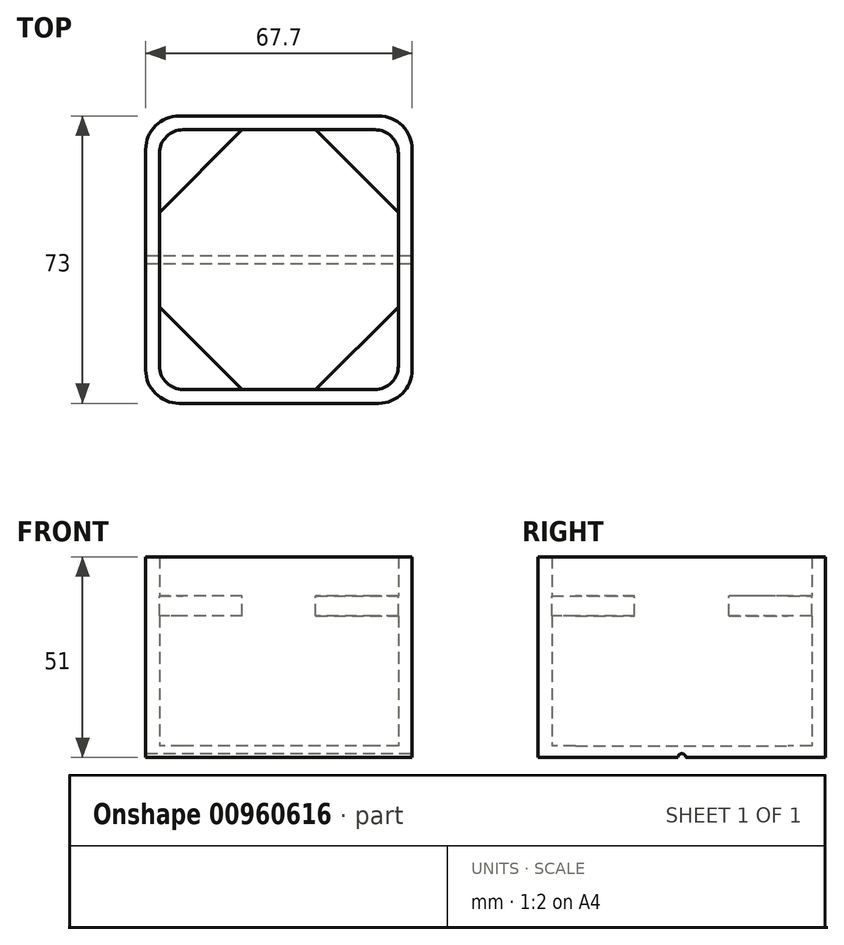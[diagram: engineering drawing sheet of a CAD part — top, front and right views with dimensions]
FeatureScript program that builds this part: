
annotation { "Feature Type Name" : "Feature", "Feature Type Description" : "" }
export const myFeature = defineFeature(function(context is Context, id is Id, definition is map)
    precondition{}
    {
        {
            var Q0;
            Q0=qCreatedBy(makeId("Top.planeOp"),FACE);
            var sketch = newSketch(context, id + "F0", { "sketchPlane" : qUnion([Q0])});
            skLineSegment(sketch, "E0.bottom", {"start": v(25.35, -36.5) * mm, "end": v(-25.35, -36.5) * mm});
            skLineSegment(sketch, "E0.top", {"start": v(25.35, 36.5) * mm, "end": v(-25.35, 36.5) * mm});
            skLineSegment(sketch, "E0.left", {"start": v(33.85, -28) * mm, "end": v(33.85, 28) * mm});
            skLineSegment(sketch, "E0.right", {"start": v(-33.85, -28) * mm, "end": v(-33.85, 28) * mm});
            skPoint(sketch, "E0.middle", {"position": v(0, 0) * mm});
            skPoint(sketch, "E1.visualSharp", {"position": v(-33.85, 36.5) * mm});
            skPoint(sketch, "E2.visualSharp", {"position": v(33.85, 36.5) * mm});
            skPoint(sketch, "E3.visualSharp", {"position": v(33.85, -36.5) * mm});
            skPoint(sketch, "E4.visualSharp", {"position": v(-33.85, -36.5) * mm});
            skArc(sketch, "E5.filletArc", {"start": v(-25.35, 36.5) * mm, "mid": v(-31.36, 34.01) * mm, "end": v(-33.85, 28) * mm});
            skArc(sketch, "E6.filletArc", {"start": v(33.85, 28) * mm, "mid": v(31.36, 34.01) * mm, "end": v(25.35, 36.5) * mm});
            skArc(sketch, "E7.filletArc", {"start": v(-33.85, -28) * mm, "mid": v(-31.36, -34.01) * mm, "end": v(-25.35, -36.5) * mm});
            skArc(sketch, "E8.filletArc", {"start": v(25.35, -36.5) * mm, "mid": v(31.36, -34.01) * mm, "end": v(33.85, -28) * mm});
            skSolve(sketch);
        }
        {
            var Q0;
            Q0=makeQuery(id+"F0.imprint","IMPRINT",FACE,{"disambiguationData":[TD([[makeQuery(id+"F0.imprint","IMPRINT",EDGE,{"derivedFrom":sQuery(id+"F0.wireOp",EDGE,"E0.bottom")}),-1.0]])]});
            extrude(context, id + "F1", {"entities" : qUnion([Q0]), "depth" : 3 * mm, "offsetDistance" : 25 * mm});
        }
        {
            var Q0;
            Q0=makeQuery(id+"F1.opExtrude","CAP_FACE",FACE,{"disambiguationData":[OSD([sQuery(id+"F0.wireOp",EDGE,"E0.bottom"),sQuery(id+"F0.wireOp",EDGE,"E0.top"),sQuery(id+"F0.wireOp",EDGE,"E0.left"),sQuery(id+"F0.wireOp",EDGE,"E0.right"),sQuery(id+"F0.wireOp",EDGE,"E1.filletArc"),sQuery(id+"F0.wireOp",EDGE,"E2.filletArc"),sQuery(id+"F0.wireOp",EDGE,"E3.filletArc"),sQuery(id+"F0.wireOp",EDGE,"E4.filletArc")])],"isStart":false});
            var sketch = newSketch(context, id + "F2", { "sketchPlane" : qUnion([Q0])});
            skLineSegment(sketch, "E9.bottom", {"start": v(24.35, -33) * mm, "end": v(-24.35, -33) * mm});
            skLineSegment(sketch, "E9.top", {"start": v(24.35, 33) * mm, "end": v(-24.35, 33) * mm});
            skLineSegment(sketch, "E9.left", {"start": v(30.35, -27) * mm, "end": v(30.35, 27) * mm});
            skLineSegment(sketch, "E9.right", {"start": v(-30.35, -27) * mm, "end": v(-30.35, 27) * mm});
            skPoint(sketch, "E9.middle", {"position": v(0, 0) * mm});
            skPoint(sketch, "E10.visualSharp", {"position": v(-30.35, 33) * mm});
            skPoint(sketch, "E11.visualSharp", {"position": v(30.35, 33) * mm});
            skPoint(sketch, "E12.visualSharp", {"position": v(-30.35, -33) * mm});
            skPoint(sketch, "E13.visualSharp", {"position": v(30.35, -33) * mm});
            skPoint(sketch, "E14", {"position": v(-22.35, 25) * mm});
            skPoint(sketch, "E15", {"position": v(22.35, 25) * mm});
            skPoint(sketch, "E16", {"position": v(22.35, -25) * mm});
            skPoint(sketch, "E17", {"position": v(-22.35, -25) * mm});
            skArc(sketch, "E18.filletArc", {"start": v(-24.35, 33) * mm, "mid": v(-28.6, 31.24) * mm, "end": v(-30.35, 27) * mm});
            skArc(sketch, "E19.filletArc", {"start": v(30.35, 27) * mm, "mid": v(28.6, 31.24) * mm, "end": v(24.35, 33) * mm});
            skArc(sketch, "E20.filletArc", {"start": v(24.35, -33) * mm, "mid": v(28.6, -31.24) * mm, "end": v(30.35, -27) * mm});
            skArc(sketch, "E21.filletArc", {"start": v(-30.35, -27) * mm, "mid": v(-28.6, -31.24) * mm, "end": v(-24.35, -33) * mm});
            skSolve(sketch);
        }
        {
            var Q0;
            Q0=makeQuery(id+"F2.imprint","IMPRINT",FACE,{"disambiguationData":[TD([[makeQuery(id+"F2.imprint","IMPRINT",EDGE,{"derivedFrom":sQuery(id+"F2.wireOp",EDGE,"E9.bottom")}),1.0]])]});
            extrude(context, id + "F3", {"entities" : qUnion([Q0]), "operationType" : NewBodyOperationType.ADD, "depth" : 38 * mm, "offsetDistance" : 25 * mm});
        }
        {
            var Q0;
            Q0=makeQuery(id+"F3.opExtrude","CAP_FACE",FACE,{"disambiguationData":[OSD([sQuery(id+"F0.wireOp",EDGE,"E0.bottom"),sQuery(id+"F0.wireOp",EDGE,"E0.top"),sQuery(id+"F0.wireOp",EDGE,"E0.left"),sQuery(id+"F0.wireOp",EDGE,"E0.right"),sQuery(id+"F0.wireOp",EDGE,"dvduAT8U-9z4F-e4AS-9eoL-lbGmKiJ1iybt"),sQuery(id+"F0.wireOp",EDGE,"aJOZrvJK-A2hF-QCfp-oE2e-V53GVGUSBUPk"),sQuery(id+"F0.wireOp",EDGE,"IG0yzDuE-LkIn-5tUI-d1jc-H29fERG7UsIG"),sQuery(id+"F0.wireOp",EDGE,"B1HQ0swq-clk5-EkSq-0daU-o4C5Dgl36Lca"),sQuery(id+"F0.wireOp",EDGE,"Mjkd7YmC-RiAe-4hFl-lhO9-aFGPjJMqciLP"),sQuery(id+"F2.wireOp",EDGE,"E9.bottom"),sQuery(id+"F2.wireOp",EDGE,"E9.top"),sQuery(id+"F2.wireOp",EDGE,"E9.left"),sQuery(id+"F2.wireOp",EDGE,"E9.right")])],"isStart":false});
            var sketch = newSketch(context, id + "F4", { "sketchPlane" : qUnion([Q0])});
            skLineSegment(sketch, "E22.bottom", {"start": v(30.35, 33) * mm, "end": v(-30.35, 33) * mm});
            skLineSegment(sketch, "E22.top", {"start": v(30.35, -33) * mm, "end": v(-30.35, -33) * mm});
            skLineSegment(sketch, "E22.left", {"start": v(30.35, 33) * mm, "end": v(30.35, -33) * mm});
            skLineSegment(sketch, "E22.right", {"start": v(-30.35, 33) * mm, "end": v(-30.35, -33) * mm});
            skPoint(sketch, "E22.middle", {"position": v(0, 0) * mm});
            skLineSegment(sketch, "E23", {"start": v(9.35, 33) * mm, "end": v(30.35, 12) * mm});
            skLineSegment(sketch, "E24", {"start": v(30.35, 12) * mm, "end": v(30.35, 27) * mm});
            skLineSegment(sketch, "E25", {"start": v(-30.35, 12) * mm, "end": v(-30.35, 27) * mm});
            skLineSegment(sketch, "E26", {"start": v(-24.35, 33) * mm, "end": v(-9.35, 33) * mm});
            skLineSegment(sketch, "E27", {"start": v(-9.35, 33) * mm, "end": v(-30.35, 12) * mm});
            skLineSegment(sketch, "E28", {"start": v(-30.35, -12) * mm, "end": v(-9.35, -33) * mm});
            skLineSegment(sketch, "E29", {"start": v(-9.35, -33) * mm, "end": v(-30.35, -33) * mm});
            skLineSegment(sketch, "E30", {"start": v(9.35, -33) * mm, "end": v(30.35, -12) * mm});
            skLineSegment(sketch, "E31", {"start": v(30.35, -12) * mm, "end": v(30.35, -27) * mm});
            skLineSegment(sketch, "E32", {"start": v(24.35, -33) * mm, "end": v(9.35, -33) * mm});
            skLineSegment(sketch, "E33", {"start": v(-30.35, -33) * mm, "end": v(-30.35, -12) * mm});
            skPoint(sketch, "E34.visualSharp", {"position": v(-30.35, 33) * mm});
            skArc(sketch, "E34.filletArc", {"start": v(-24.35, 33) * mm, "mid": v(-28.6, 31.24) * mm, "end": v(-30.35, 27) * mm});
            skPoint(sketch, "E35.visualSharp", {"position": v(30.35, -33) * mm});
            skArc(sketch, "E35.filletArc", {"start": v(24.35, -33) * mm, "mid": v(28.6, -31.24) * mm, "end": v(30.35, -27) * mm});
            skLineSegment(sketch, "E36", {"start": v(9.35, 33) * mm, "end": v(24.35, 33) * mm});
            skPoint(sketch, "E37.visualSharp", {"position": v(30.35, 33) * mm});
            skArc(sketch, "E37.filletArc", {"start": v(30.35, 27) * mm, "mid": v(28.6, 31.24) * mm, "end": v(24.35, 33) * mm});
            skLineSegment(sketch, "E38", {"start": v(-30.35, -12) * mm, "end": v(-30.35, -27) * mm});
            skLineSegment(sketch, "E39", {"start": v(-24.35, -33) * mm, "end": v(-9.35, -33) * mm});
            skPoint(sketch, "E40.visualSharp", {"position": v(-30.35, -33) * mm});
            skArc(sketch, "E40.filletArc", {"start": v(-30.35, -27) * mm, "mid": v(-28.6, -31.24) * mm, "end": v(-24.35, -33) * mm});
            skSolve(sketch);
        }
        {
            var Q0;
            Q0 = qSketchRegion(id + "F6", true);
            var Q1;
            Q1=makeQuery(id+"F4.imprint","IMPRINT",FACE,{"disambiguationData":[TD([[makeQuery(id+"F4.imprint","IMPRINT",EDGE,{"derivedFrom":makeQuery(id+"F3.opExtrude","CAP_EDGE",EDGE,{"disambiguationData":[OSD([sQuery(id+"F0.wireOp",EDGE,"E0.bottom")])],"isStart":false})}),-1.0]])]});
            var Q2;
            {var subQ0=sQuery(id+"F4.wireOp",EDGE,"E34.filletArc");Q2=makeQuery(id+"F4.imprint","IMPRINT",FACE,{"disambiguationData":[TD([[makeQuery(id+"F4.imprint","IMPRINT",EDGE,{"derivedFrom":subQ0}),-1.0]])]});}
            var Q3;
            {var subQ0=sQuery(id+"F4.wireOp",EDGE,"E37.filletArc");Q3=makeQuery(id+"F4.imprint","IMPRINT",FACE,{"disambiguationData":[TD([[makeQuery(id+"F4.imprint","IMPRINT",EDGE,{"derivedFrom":subQ0}),-1.0]])]});}
            var Q4;
            {var subQ0=sQuery(id+"F4.wireOp",EDGE,"E35.filletArc");Q4=makeQuery(id+"F4.imprint","IMPRINT",FACE,{"disambiguationData":[TD([[makeQuery(id+"F4.imprint","IMPRINT",EDGE,{"derivedFrom":subQ0}),-1.0]])]});}
            var Q5;
            {var subQ0=sQuery(id+"F4.wireOp",EDGE,"E40.filletArc");Q5=makeQuery(id+"F4.imprint","IMPRINT",FACE,{"disambiguationData":[TD([[makeQuery(id+"F4.imprint","IMPRINT",EDGE,{"derivedFrom":subQ0}),-1.0]])]});}
            var Q6;
            {var subQ2=sQuery(id+"F4.wireOp",EDGE,"E30");Q6=makeQuery(id+"F4.imprint","IMPRINT",FACE,{"disambiguationData":[TD([[makeQuery(id+"F4.imprint","IMPRINT",EDGE,{"derivedFrom":subQ2}),-1.0]])]});}
            var Q7;
            {var subQ2=sQuery(id+"F4.wireOp",EDGE,"E23");Q7=makeQuery(id+"F4.imprint","IMPRINT",FACE,{"disambiguationData":[TD([[makeQuery(id+"F4.imprint","IMPRINT",EDGE,{"derivedFrom":subQ2}),1.0]])]});}
            var Q8;
            {var subQ2=sQuery(id+"F4.wireOp",EDGE,"E27");Q8=makeQuery(id+"F4.imprint","IMPRINT",FACE,{"disambiguationData":[TD([[makeQuery(id+"F4.imprint","IMPRINT",EDGE,{"derivedFrom":subQ2}),-1.0]])]});}
            var Q9;
            {var subQ2=sQuery(id+"F4.wireOp",EDGE,"E28");Q9=makeQuery(id+"F4.imprint","IMPRINT",FACE,{"disambiguationData":[TD([[makeQuery(id+"F4.imprint","IMPRINT",EDGE,{"derivedFrom":subQ2}),-1.0]])]});}
            extrude(context, id + "F5", {"entities" : qUnion([Q0, Q1, Q2, Q3, Q4, Q5, Q6, Q7, Q8, Q9]), "operationType" : NewBodyOperationType.ADD, "oppositeDirection" : true, "depth" : 5 * mm, "offsetDistance" : 25 * mm});
        }
        {
            var Q0;
            {var subQ0=sQuery(id+"F0.wireOp",EDGE,"E8.filletArc");var subQ1=sQuery(id+"F0.wireOp",EDGE,"E7.filletArc");var subQ2=sQuery(id+"F0.wireOp",EDGE,"E6.filletArc");var subQ3=sQuery(id+"F0.wireOp",EDGE,"E5.filletArc");var subQ4=sQuery(id+"F0.wireOp",EDGE,"E0.right");var subQ5=sQuery(id+"F0.wireOp",EDGE,"E0.left");var subQ6=sQuery(id+"F0.wireOp",EDGE,"E0.top");var subQ7=sQuery(id+"F0.wireOp",EDGE,"E0.bottom");Q0=makeQuery(id+"F5.boolean.opBoolean","MERGE",FACE,{"derivedFrom":[makeQuery(id+"F3.opExtrude","CAP_FACE",FACE,{"disambiguationData":[OSD([subQ7,subQ6,subQ5,subQ4,subQ3,subQ2,subQ1,subQ0,sQuery(id+"F2.wireOp",EDGE,"E9.bottom"),sQuery(id+"F2.wireOp",EDGE,"E9.top"),sQuery(id+"F2.wireOp",EDGE,"E9.left"),sQuery(id+"F2.wireOp",EDGE,"E9.right"),sQuery(id+"F2.wireOp",EDGE,"E18.filletArc"),sQuery(id+"F2.wireOp",EDGE,"E19.filletArc"),sQuery(id+"F2.wireOp",EDGE,"E20.filletArc"),sQuery(id+"F2.wireOp",EDGE,"E21.filletArc")])],"isStart":false}),makeQuery(id+"F5.opExtrude","CAP_FACE",FACE,{"disambiguationData":[OSD([subQ7,subQ6,subQ5,subQ4,subQ3,subQ2,subQ1,subQ0,sQuery(id+"F4.wireOp",EDGE,"E22.bottom"),sQuery(id+"F4.wireOp",EDGE,"E22.top"),sQuery(id+"F4.wireOp",EDGE,"E22.left"),sQuery(id+"F4.wireOp",EDGE,"E22.right"),sQuery(id+"F4.wireOp",EDGE,"E23"),sQuery(id+"F4.wireOp",EDGE,"E27"),sQuery(id+"F4.wireOp",EDGE,"E28"),sQuery(id+"F4.wireOp",EDGE,"E30")])],"isStart":true})]});}
            var sketch = newSketch(context, id + "F6", { "sketchPlane" : qUnion([Q0])});
            skLineSegment(sketch, "E41.bottom", {"start": v(24.35, 33) * mm, "end": v(-24.35, 33) * mm});
            skLineSegment(sketch, "E41.top", {"start": v(24.35, -33) * mm, "end": v(-24.35, -33) * mm});
            skLineSegment(sketch, "E41.left", {"start": v(30.35, 27) * mm, "end": v(30.35, -27) * mm});
            skLineSegment(sketch, "E41.right", {"start": v(-30.35, 27) * mm, "end": v(-30.35, -27) * mm});
            skPoint(sketch, "E41.middle", {"position": v(0, 0) * mm});
            skPoint(sketch, "E42.visualSharp", {"position": v(-30.35, 33) * mm});
            skArc(sketch, "E42.filletArc", {"start": v(-24.35, 33) * mm, "mid": v(-28.6, 31.24) * mm, "end": v(-30.35, 27) * mm});
            skPoint(sketch, "E43.visualSharp", {"position": v(30.35, 33) * mm});
            skArc(sketch, "E43.filletArc", {"start": v(30.35, 27) * mm, "mid": v(28.6, 31.24) * mm, "end": v(24.35, 33) * mm});
            skPoint(sketch, "E44.visualSharp", {"position": v(-30.35, -33) * mm});
            skArc(sketch, "E44.filletArc", {"start": v(-30.35, -27) * mm, "mid": v(-28.6, -31.24) * mm, "end": v(-24.35, -33) * mm});
            skPoint(sketch, "E45.visualSharp", {"position": v(30.35, -33) * mm});
            skArc(sketch, "E45.filletArc", {"start": v(24.35, -33) * mm, "mid": v(28.6, -31.24) * mm, "end": v(30.35, -27) * mm});
            skSolve(sketch);
        }
        {
            var Q0;
            {var subQ3=sQuery(id+"F6.wireOp",EDGE,"E42.filletArc");Q0=makeQuery(id+"F6.imprint","IMPRINT",FACE,{"disambiguationData":[TD([[makeQuery(id+"F6.imprint","IMPRINT",EDGE,{"derivedFrom":subQ3}),-1.0]])]});}
            extrude(context, id + "F7", {"entities" : qUnion([Q0]), "operationType" : NewBodyOperationType.ADD, "depth" : 10 * mm, "offsetDistance" : 25 * mm});
        }
        {
            var Q0;
            {var subQ0=sQuery(id+"F0.wireOp",EDGE,"E0.left");Q0=makeQuery(id+"F7.boolean.opBoolean","MERGE",FACE,{"derivedFrom":[makeQuery(id+"F3.boolean.opBoolean","MERGE",FACE,{"derivedFrom":[makeQuery(id+"F1.opExtrude","SWEPT_FACE",FACE,{"disambiguationData":[OSD([subQ0])]}),makeQuery(id+"F3.opExtrude","SWEPT_FACE",FACE,{"disambiguationData":[OSD([subQ0])]})]}),makeQuery(id+"F7.opExtrude","SWEPT_FACE",FACE,{"disambiguationData":[OSD([subQ0])]})]});}
            var sketch = newSketch(context, id + "F8", { "sketchPlane" : qUnion([Q0])});
            skCircle(sketch, "E46", {"center": v(0, 0) * mm, "radius": 1 * mm});
            skSolve(sketch);
        }
        {
            var Q0;
            {var subQ0=sQuery(id+"F8.wireOp",EDGE,"E46");var subQ1=makeQuery(id+"F1.opExtrude","CAP_EDGE",EDGE,{"disambiguationData":[OSD([sQuery(id+"F0.wireOp",EDGE,"E0.left")])],"isStart":true});var subQ2=makeQuery(id+"F8.imprint","INTERSECT",VERTEX,{"disambiguationData":[OD(0.0)],"derivedFrom":[subQ1,subQ0]});Q0=makeQuery(id+"F8.imprint","IMPRINT",FACE,{"disambiguationData":[TD([[makeQuery(id+"F8.imprint","IMPRINT",EDGE,{"disambiguationData":[TD([[subQ2,1.0]])],"derivedFrom":subQ0}),1.0]])]});}
            extrude(context, id + "F9", {"entities" : qUnion([Q0]), "operationType" : NewBodyOperationType.REMOVE, "endBound" : BoundingType.THROUGH_ALL, "oppositeDirection" : true, "depth" : 25 * mm, "offsetDistance" : 25 * mm});
        }
    });
